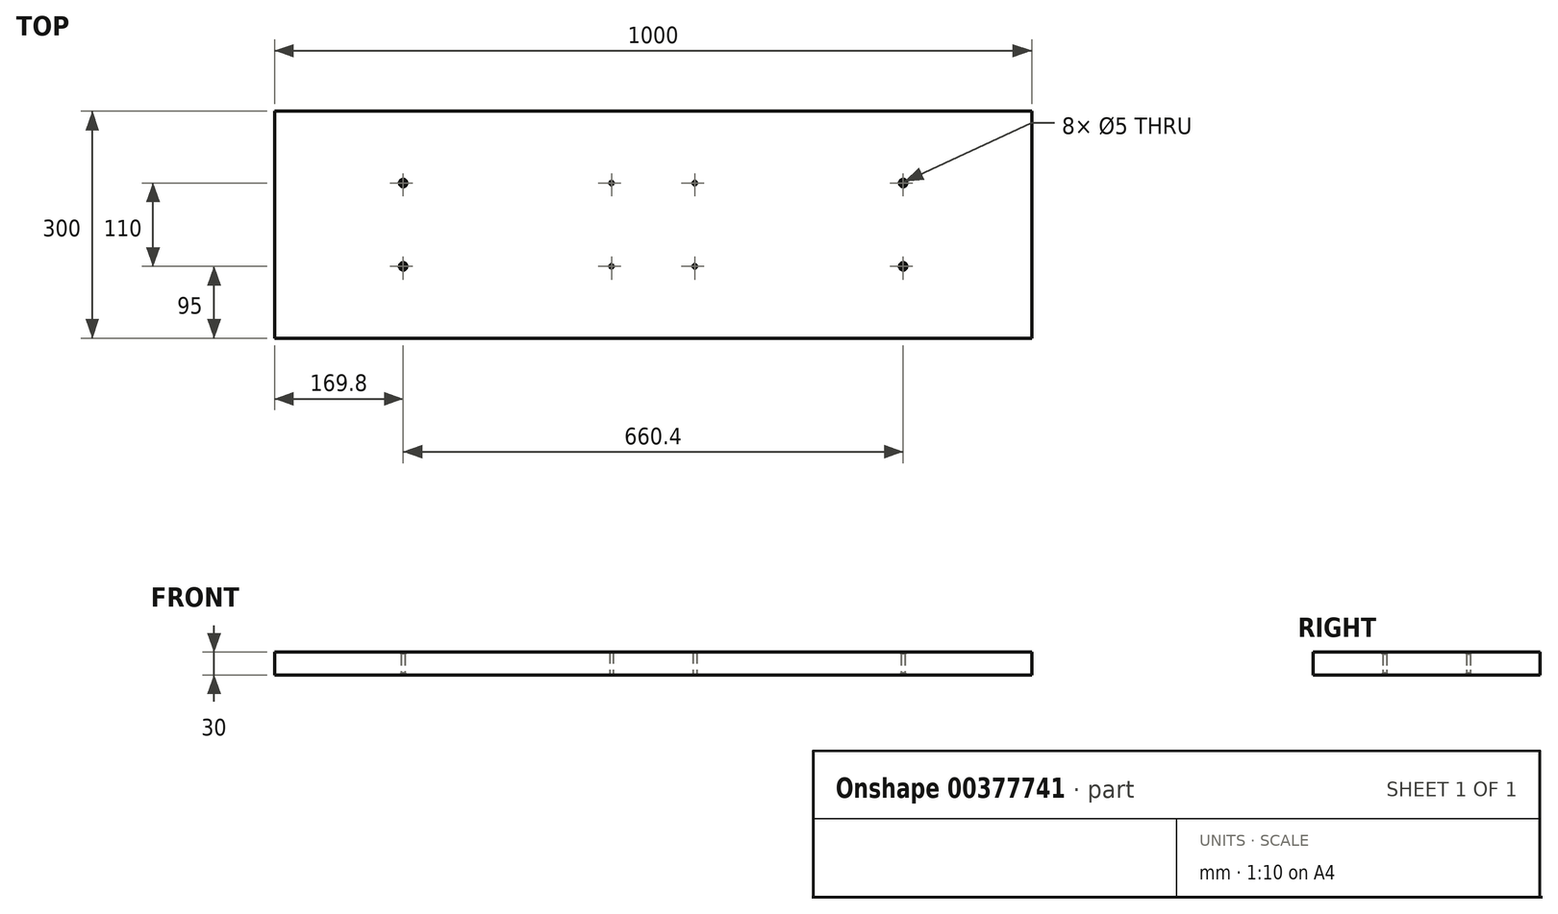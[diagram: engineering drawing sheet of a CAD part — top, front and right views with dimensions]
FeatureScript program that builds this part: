
annotation { "Feature Type Name" : "Feature", "Feature Type Description" : "" }
export const myFeature = defineFeature(function(context is Context, id is Id, definition is map)
    precondition{}
    {
        {
            var Q0;
            Q0=qCreatedBy(makeId("Top.planeOp"),FACE);
            var sketch = newSketch(context, id + "F0", { "sketchPlane" : qUnion([Q0])});
            skLineSegment(sketch, "E0.bottom", {"start": v(500, -150) * mm, "end": v(-500, -150) * mm});
            skLineSegment(sketch, "E0.top", {"start": v(500, 150) * mm, "end": v(-500, 150) * mm});
            skLineSegment(sketch, "E0.left", {"start": v(500, -150) * mm, "end": v(500, 150) * mm});
            skLineSegment(sketch, "E0.right", {"start": v(-500, -150) * mm, "end": v(-500, 150) * mm});
            skPoint(sketch, "E0.middle", {"position": v(0, 0) * mm});
            skLineSegment(sketch, "E1.bottom", {"start": v(330.2, -55) * mm, "end": v(-330.2, -55) * mm, "construction": true});
            skLineSegment(sketch, "E1.top", {"start": v(330.2, 55) * mm, "end": v(-330.2, 55) * mm, "construction": true});
            skLineSegment(sketch, "E1.left", {"start": v(330.2, -55) * mm, "end": v(330.2, 55) * mm, "construction": true});
            skLineSegment(sketch, "E1.right", {"start": v(-330.2, -55) * mm, "end": v(-330.2, 55) * mm, "construction": true});
            skCircle(sketch, "E2", {"center": v(-330.2, 55) * mm, "radius": 2.5 * mm});
            skLineSegment(sketch, "E3", {"start": v(0, 150) * mm, "end": v(0, -150) * mm, "construction": true});
            skCircle(sketch, "E4.MirrorC", {"center": v(330.2, 55) * mm, "radius": 2.5 * mm});
            skLineSegment(sketch, "E5", {"start": v(-500, 0) * mm, "end": v(500, 0) * mm, "construction": true});
            skCircle(sketch, "E6.MirrorC", {"center": v(330.2, -55) * mm, "radius": 2.5 * mm});
            skCircle(sketch, "E7.MirrorC", {"center": v(-330.2, -55) * mm, "radius": 2.5 * mm});
            skLineSegment(sketch, "E8.bottom", {"start": v(55, -55) * mm, "end": v(-55, -55) * mm, "construction": true});
            skLineSegment(sketch, "E8.top", {"start": v(55, 55) * mm, "end": v(-55, 55) * mm, "construction": true});
            skLineSegment(sketch, "E8.left", {"start": v(55, -55) * mm, "end": v(55, 55) * mm, "construction": true});
            skLineSegment(sketch, "E8.right", {"start": v(-55, -55) * mm, "end": v(-55, 55) * mm, "construction": true});
            skCircle(sketch, "E9", {"center": v(-55, 55) * mm, "radius": 2.5 * mm});
            skCircle(sketch, "E10.MirrorC", {"center": v(55, 55) * mm, "radius": 2.5 * mm});
            skCircle(sketch, "E11.MirrorC", {"center": v(55, -55) * mm, "radius": 2.5 * mm});
            skCircle(sketch, "E12.MirrorC", {"center": v(-55, -55) * mm, "radius": 2.5 * mm});
            skSolve(sketch);
        }
        {
            var Q0;
            Q0=makeQuery(id+"F0.imprint","IMPRINT",FACE,{"disambiguationData":[TD([[makeQuery(id+"F0.imprint","IMPRINT",EDGE,{"derivedFrom":sQuery(id+"F0.wireOp",EDGE,"E0.bottom")}),-1.0]])]});
            extrude(context, id + "F1", {"entities" : qUnion([Q0]), "depth" : 30 * mm});
        }
        {
            var Q0;
            Q0=makeQuery(id+"F1.opExtrude","CAP_EDGE",EDGE,{"disambiguationData":[OSD([sQuery(id+"F0.wireOp",EDGE,"E2")])],"isStart":false});
            var Q1;
            Q1=makeQuery(id+"F1.opExtrude","CAP_EDGE",EDGE,{"disambiguationData":[OSD([sQuery(id+"F0.wireOp",EDGE,"E7.MirrorC")])],"isStart":false});
            var Q2;
            Q2=makeQuery(id+"F1.opExtrude","CAP_EDGE",EDGE,{"disambiguationData":[OSD([sQuery(id+"F0.wireOp",EDGE,"E4.MirrorC")])],"isStart":false});
            var Q3;
            Q3=makeQuery(id+"F1.opExtrude","CAP_EDGE",EDGE,{"disambiguationData":[OSD([sQuery(id+"F0.wireOp",EDGE,"E6.MirrorC")])],"isStart":false});
            chamfer(context, id + "F2", {"entities" : qUnion([Q0, Q1, Q2, Q3]), "width" : 2.5 * mm, "tangentPropagation" : true});
        }
        {
            var Q0;
            Q0=makeQuery(id+"F1.opExtrude","CAP_EDGE",EDGE,{"disambiguationData":[OSD([sQuery(id+"F0.wireOp",EDGE,"E7.MirrorC")])],"isStart":true});
            var Q1;
            Q1=makeQuery(id+"F1.opExtrude","CAP_EDGE",EDGE,{"disambiguationData":[OSD([sQuery(id+"F0.wireOp",EDGE,"E2")])],"isStart":true});
            var Q2;
            Q2=makeQuery(id+"F1.opExtrude","CAP_EDGE",EDGE,{"disambiguationData":[OSD([sQuery(id+"F0.wireOp",EDGE,"E6.MirrorC")])],"isStart":true});
            var Q3;
            Q3=makeQuery(id+"F1.opExtrude","CAP_EDGE",EDGE,{"disambiguationData":[OSD([sQuery(id+"F0.wireOp",EDGE,"E4.MirrorC")])],"isStart":true});
            chamfer(context, id + "F3", {"entities" : qUnion([Q0, Q1, Q2, Q3]), "width" : 2.5 * mm, "tangentPropagation" : true});
        }
    });
